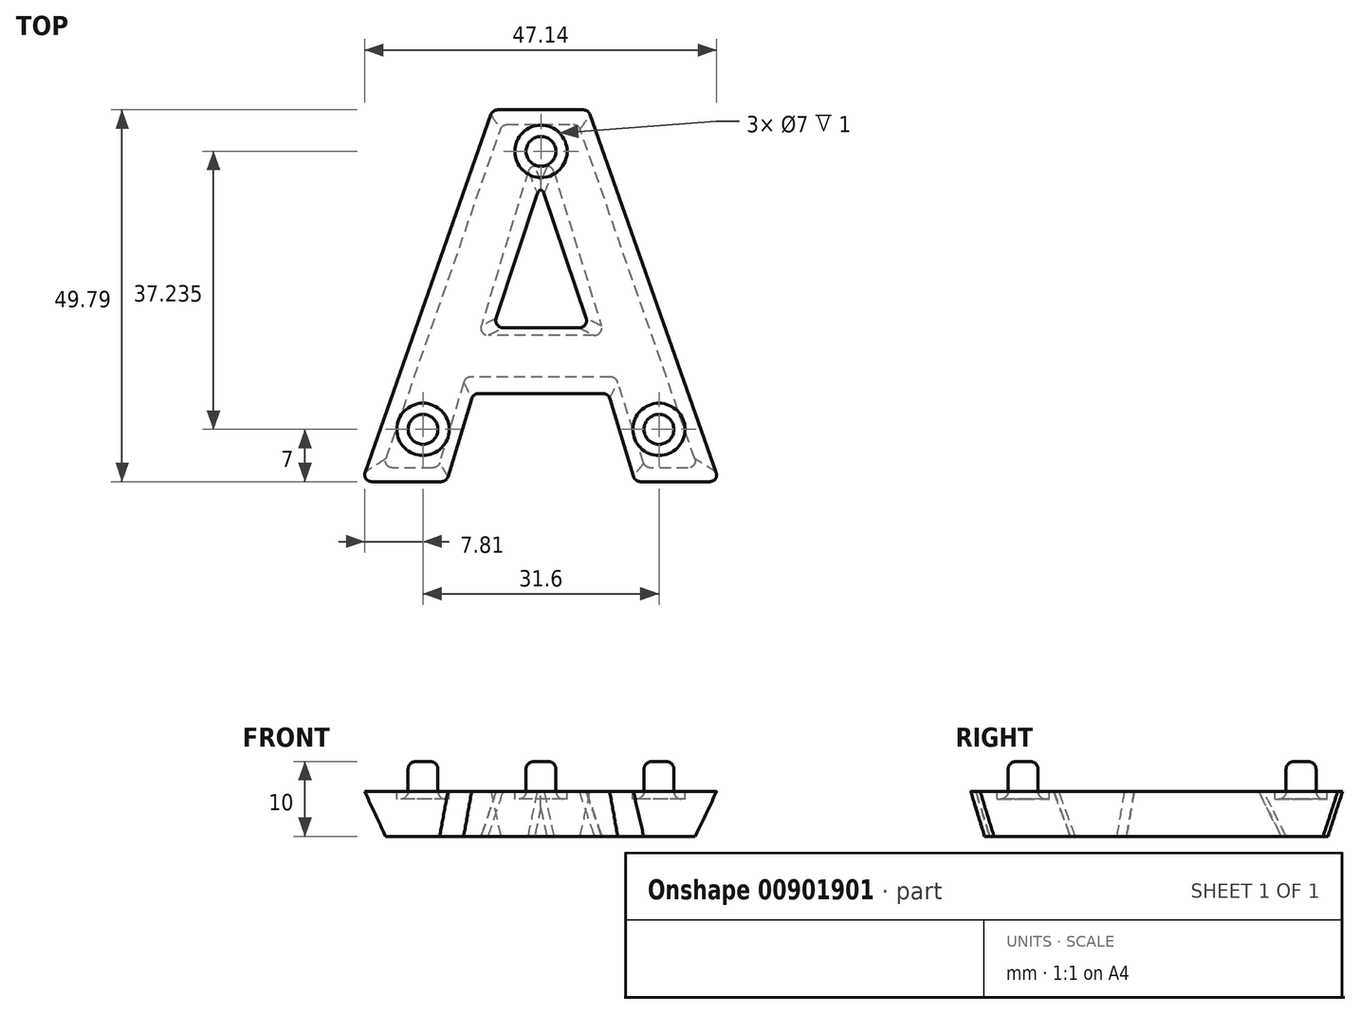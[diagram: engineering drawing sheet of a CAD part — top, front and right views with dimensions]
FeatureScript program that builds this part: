
annotation { "Feature Type Name" : "Feature", "Feature Type Description" : "" }
export const myFeature = defineFeature(function(context is Context, id is Id, definition is map)
    precondition{}
    {
        {
            var Q0;
            Q0=qCreatedBy(makeId("Top.planeOp"),FACE);
            cPlane(context, id + "F0", {"entities" : qUnion([Q0]), "cplaneType" : CPlaneType.OFFSET, "offset" : 6 * mm, "width" : 150 * mm, "height" : 150 * mm});
        }
        {
            var Q0;
            Q0=qCreatedBy(id+"F0.planeOp",FACE);
            var sketch = newSketch(context, id + "F1", { "sketchPlane" : qUnion([Q0])});
            skLineSegment(sketch, "E0", {"start": v(0, 0) * mm, "end": v(17.51, 49.8) * mm});
            skLineSegment(sketch, "E1", {"start": v(17.51, 49.8) * mm, "end": v(30.34, 49.8) * mm});
            skLineSegment(sketch, "E2", {"start": v(30.34, 49.8) * mm, "end": v(47.92, 0) * mm});
            skLineSegment(sketch, "E3", {"start": v(47.92, 0) * mm, "end": v(36.59, 0) * mm});
            skLineSegment(sketch, "E4", {"start": v(36.59, 0) * mm, "end": v(33, 11.8) * mm});
            skLineSegment(sketch, "E5", {"start": v(33, 11.8) * mm, "end": v(14.92, 11.8) * mm});
            skLineSegment(sketch, "E6", {"start": v(14.92, 11.8) * mm, "end": v(11.34, 0) * mm});
            skLineSegment(sketch, "E7", {"start": v(11.34, 0) * mm, "end": v(0, 0) * mm});
            skPoint(sketch, "E8.end.orphan", {"position": v(23.97, 42.08) * mm});
            skSolve(sketch);
        }
        {
            var Q0;
            Q0=qCreatedBy(makeId("Top.planeOp"),FACE);
            var sketch = newSketch(context, id + "F2", { "sketchPlane" : qUnion([Q0])});
            skLineSegment(sketch, "E9", {"start": v(45.03, 1.84) * mm, "end": v(37.97, 1.84) * mm});
            skLineSegment(sketch, "E10", {"start": v(37.97, 1.84) * mm, "end": v(34.05, 14) * mm});
            skLineSegment(sketch, "E11", {"start": v(34.05, 14) * mm, "end": v(13.85, 14) * mm});
            skLineSegment(sketch, "E12", {"start": v(13.85, 14) * mm, "end": v(10.22, 1.84) * mm});
            skLineSegment(sketch, "E13", {"start": v(10.22, 1.84) * mm, "end": v(2.8, 1.84) * mm});
            skLineSegment(sketch, "E14", {"start": v(2.8, 1.84) * mm, "end": v(18.82, 47.84) * mm});
            skLineSegment(sketch, "E15", {"start": v(18.82, 47.84) * mm, "end": v(29.02, 47.84) * mm});
            skLineSegment(sketch, "E16", {"start": v(45.03, 1.84) * mm, "end": v(29.02, 47.84) * mm});
            skLineSegment(sketch, "E17", {"start": v(37.97, 1.84) * mm, "end": v(34.05, 14) * mm, "construction": true});
            skSolve(sketch);
        }
        {
            var Q0;
            Q0=qCreatedBy(id+"F0.planeOp",FACE);
            cPlane(context, id + "F3", {"entities" : qUnion([Q0]), "cplaneType" : CPlaneType.OFFSET, "offset" : 5 * mm, "width" : 150 * mm, "height" : 150 * mm});
        }
        {
            var Q0;
            Q0=qCreatedBy(makeId("Top.planeOp"),FACE);
            cPlane(context, id + "F4", {"entities" : qUnion([Q0]), "cplaneType" : CPlaneType.OFFSET, "offset" : 5 * mm, "oppositeDirection" : true, "width" : 150 * mm, "height" : 150 * mm});
        }
        {
            var Q0;
            Q0=makeQuery(id+"F1.imprint","IMPRINT",FACE,{"disambiguationData":[TD([[makeQuery(id+"F1.imprint","IMPRINT",EDGE,{"derivedFrom":sQuery(id+"F1.wireOp",EDGE,"E0")}),-1.0]])]});
            var Q1;
            Q1=makeQuery(id+"F2.imprint","IMPRINT",FACE,{"disambiguationData":[TD([[makeQuery(id+"F2.imprint","IMPRINT",EDGE,{"derivedFrom":sQuery(id+"F2.wireOp",EDGE,"E9")}),-1.0]])]});
            loft(context, id + "F5", {"sheetProfilesArray" : [{ "sheetProfileEntities" : qUnion([Q0]) }, { "sheetProfileEntities" : qUnion([Q1]) }]});
        }
        {
            var Q0;
            Q0=makeQuery(id+"F1.imprint","IMPRINT",FACE,{"disambiguationData":[TD([[makeQuery(id+"F1.imprint","IMPRINT",EDGE,{"derivedFrom":sQuery(id+"F1.wireOp",EDGE,"E0")}),-1.0]])]});
            var sketch = newSketch(context, id + "F6", { "sketchPlane" : qUnion([Q0])});
            skLineSegment(sketch, "E18", {"start": v(17.57, 20.6) * mm, "end": v(30.48, 20.6) * mm});
            skLineSegment(sketch, "E19", {"start": v(30.48, 20.6) * mm, "end": v(24.2, 39.24) * mm});
            skLineSegment(sketch, "E20", {"start": v(23.75, 39.24) * mm, "end": v(17.57, 20.6) * mm});
            skLineSegment(sketch, "E21", {"start": v(23.75, 39.24) * mm, "end": v(24.2, 39.24) * mm});
            skSolve(sketch);
        }
        {
            var Q0;
            Q0=makeQuery(id+"F2.imprint","IMPRINT",FACE,{"disambiguationData":[TD([[makeQuery(id+"F2.imprint","IMPRINT",EDGE,{"derivedFrom":sQuery(id+"F2.wireOp",EDGE,"E9")}),-1.0]])]});
            var sketch = newSketch(context, id + "F7", { "sketchPlane" : qUnion([Q0])});
            skLineSegment(sketch, "E22", {"start": v(32.48, 19.6) * mm, "end": v(15.62, 19.6) * mm});
            skLineSegment(sketch, "E23", {"start": v(22.5, 42.24) * mm, "end": v(25.5, 42.24) * mm});
            skLineSegment(sketch, "E24", {"start": v(24, 42.24) * mm, "end": v(24, 15.1) * mm, "construction": true});
            skLineSegment(sketch, "E25", {"start": v(25.5, 42.24) * mm, "end": v(37.96, 1.84) * mm, "construction": true});
            skLineSegment(sketch, "E26", {"start": v(22.5, 42.24) * mm, "end": v(8.33, -4.36) * mm, "construction": true});
            skPoint(sketch, "E27.end.orphan", {"position": v(31.77, 19.6) * mm});
            skPoint(sketch, "E28.start.orphan", {"position": v(16.2, 19.6) * mm});
            skLineSegment(sketch, "E29", {"start": v(25.5, 42.24) * mm, "end": v(32.48, 19.6) * mm});
            skLineSegment(sketch, "E30", {"start": v(22.5, 42.24) * mm, "end": v(15.62, 19.6) * mm});
            skSolve(sketch);
        }
        {
            var Q0;
            Q0=makeQuery(id+"F7.imprint","IMPRINT",FACE,{"disambiguationData":[TD([[makeQuery(id+"F7.imprint","IMPRINT",EDGE,{"derivedFrom":sQuery(id+"F7.wireOp",EDGE,"E22")}),-1.0]])]});
            var Q1;
            Q1=makeQuery(id+"F6.imprint","IMPRINT",FACE,{"disambiguationData":[TD([[makeQuery(id+"F6.imprint","IMPRINT",EDGE,{"derivedFrom":sQuery(id+"F6.wireOp",EDGE,"E18")}),1.0]])]});
            loft(context, id + "F8", {"operationType" : NewBodyOperationType.REMOVE, "sheetProfilesArray" : [{ "sheetProfileEntities" : qUnion([Q0]) }, { "sheetProfileEntities" : qUnion([Q1]) }]});
        }
        {
            var Q0;
            Q0=makeQuery(id+"F1.imprint","IMPRINT",FACE,{"disambiguationData":[TD([[makeQuery(id+"F1.imprint","IMPRINT",EDGE,{"derivedFrom":sQuery(id+"F1.wireOp",EDGE,"E0")}),-1.0]])]});
            var sketch = newSketch(context, id + "F9", { "sketchPlane" : qUnion([Q0])});
            skCircle(sketch, "E31", {"center": v(24, 44.24) * mm, "radius": 3.5 * mm});
            skCircle(sketch, "E32", {"center": v(8.2, 7) * mm, "radius": 3.5 * mm});
            skCircle(sketch, "E33", {"center": v(39.8, 7) * mm, "radius": 3.5 * mm});
            skCircle(sketch, "E34", {"center": v(24, 44.24) * mm, "radius": 2 * mm});
            skCircle(sketch, "E35", {"center": v(39.8, 7) * mm, "radius": 2 * mm});
            skCircle(sketch, "E36", {"center": v(8.2, 7) * mm, "radius": 2 * mm});
            skSolve(sketch);
        }
        {
            var Q0;
            Q0=makeQuery(id+"F9.imprint","IMPRINT",FACE,{"disambiguationData":[TD([[makeQuery(id+"F9.imprint","IMPRINT",EDGE,{"derivedFrom":sQuery(id+"F9.wireOp",EDGE,"E36")}),1.0]])]});
            var Q1;
            Q1=makeQuery(id+"F9.imprint","IMPRINT",FACE,{"disambiguationData":[TD([[makeQuery(id+"F9.imprint","IMPRINT",EDGE,{"derivedFrom":sQuery(id+"F9.wireOp",EDGE,"E34")}),1.0]])]});
            var Q2;
            Q2=makeQuery(id+"F9.imprint","IMPRINT",FACE,{"disambiguationData":[TD([[makeQuery(id+"F9.imprint","IMPRINT",EDGE,{"derivedFrom":sQuery(id+"F9.wireOp",EDGE,"E35")}),1.0]])]});
            var Q3;
            Q3=sQuery(id+"F9.wireOp",EDGE,"E36");
            var Q4;
            Q4=sQuery(id+"F9.wireOp",EDGE,"E34");
            var Q5;
            Q5=sQuery(id+"F9.wireOp",EDGE,"E35");
            extrude(context, id + "F10", {"entities" : qUnion([Q0, Q1, Q2]), "operationType" : NewBodyOperationType.ADD, "surfaceEntities" : qUnion([Q3, Q4, Q5]), "depth" : 4 * mm, "offsetDistance" : 25 * mm});
        }
        {
            var Q0;
            Q0=makeQuery(id+"F9.imprint","IMPRINT",FACE,{"disambiguationData":[TD([[makeQuery(id+"F9.imprint","IMPRINT",EDGE,{"derivedFrom":sQuery(id+"F9.wireOp",EDGE,"E32")}),1.0]])]});
            var Q1;
            Q1=sQuery(id+"F9.wireOp",EDGE,"E36");
            var Q2;
            Q2=sQuery(id+"F9.wireOp",EDGE,"E32");
            extrude(context, id + "F11", {"entities" : qUnion([Q0]), "operationType" : NewBodyOperationType.REMOVE, "surfaceEntities" : qUnion([Q1, Q2]), "oppositeDirection" : true, "depth" : 1 * mm, "offsetDistance" : 25 * mm});
        }
        {
            var Q0;
            Q0=makeQuery(id+"F9.imprint","IMPRINT",FACE,{"disambiguationData":[TD([[makeQuery(id+"F9.imprint","IMPRINT",EDGE,{"derivedFrom":sQuery(id+"F9.wireOp",EDGE,"E33")}),1.0]])]});
            var Q1;
            Q1=sQuery(id+"F9.wireOp",EDGE,"E35");
            var Q2;
            Q2=sQuery(id+"F9.wireOp",EDGE,"E33");
            extrude(context, id + "F12", {"entities" : qUnion([Q0]), "operationType" : NewBodyOperationType.REMOVE, "surfaceEntities" : qUnion([Q1, Q2]), "oppositeDirection" : true, "depth" : 1 * mm, "offsetDistance" : 25 * mm});
        }
        {
            var Q0;
            Q0=makeQuery(id+"F9.imprint","IMPRINT",FACE,{"disambiguationData":[TD([[makeQuery(id+"F9.imprint","IMPRINT",EDGE,{"derivedFrom":sQuery(id+"F9.wireOp",EDGE,"E31")}),1.0]])]});
            var Q1;
            Q1=sQuery(id+"F9.wireOp",EDGE,"E34");
            var Q2;
            Q2=sQuery(id+"F9.wireOp",EDGE,"E31");
            extrude(context, id + "F13", {"entities" : qUnion([Q0]), "operationType" : NewBodyOperationType.REMOVE, "surfaceEntities" : qUnion([Q1, Q2]), "oppositeDirection" : true, "depth" : 1 * mm, "offsetDistance" : 25 * mm});
        }
        {
            var Q0;
            Q0=makeQuery(id+"F11.boolean.opBoolean","COPY",EDGE,{"derivedFrom":makeQuery(id+"F11.opExtrude","CAP_EDGE",EDGE,{"disambiguationData":[OSD([sQuery(id+"F9.wireOp",EDGE,"E36")])],"isStart":false})});
            fillet(context, id + "F14", {"entities" : qUnion([Q0]), "tangentPropagation" : true, "radius" : 1 * mm, "defaultsChanged" : false, "vertexSettings" : [], "allowEdgeOverflow" : false});
        }
        {
            var Q0;
            Q0=makeQuery(id+"F10.opExtrude","CAP_EDGE",EDGE,{"disambiguationData":[OSD([sQuery(id+"F9.wireOp",EDGE,"E36")])],"isStart":false});
            fillet(context, id + "F15", {"entities" : qUnion([Q0]), "tangentPropagation" : true, "radius" : 1 * mm, "defaultsChanged" : true, "vertexSettings" : [], "allowEdgeOverflow" : false});
        }
        {
            var Q0;
            Q0=makeQuery(id+"F10.opExtrude","CAP_EDGE",EDGE,{"disambiguationData":[OSD([sQuery(id+"F9.wireOp",EDGE,"E35")])],"isStart":false});
            fillet(context, id + "F16", {"entities" : qUnion([Q0]), "tangentPropagation" : true, "radius" : 1 * mm, "defaultsChanged" : true, "vertexSettings" : [], "allowEdgeOverflow" : false});
        }
        {
            var Q0;
            Q0=makeQuery(id+"F10.opExtrude","CAP_EDGE",EDGE,{"disambiguationData":[OSD([sQuery(id+"F9.wireOp",EDGE,"E34")])],"isStart":false});
            fillet(context, id + "F17", {"entities" : qUnion([Q0]), "tangentPropagation" : true, "radius" : 1 * mm, "defaultsChanged" : true, "vertexSettings" : [], "allowEdgeOverflow" : false});
        }
        {
            var Q0;
            Q0=makeQuery(id+"F13.boolean.opBoolean","COPY",EDGE,{"derivedFrom":makeQuery(id+"F13.opExtrude","CAP_EDGE",EDGE,{"disambiguationData":[OSD([sQuery(id+"F9.wireOp",EDGE,"E34")])],"isStart":false})});
            fillet(context, id + "F18", {"entities" : qUnion([Q0]), "tangentPropagation" : true, "radius" : 1 * mm, "defaultsChanged" : true, "vertexSettings" : [], "allowEdgeOverflow" : false});
        }
        {
            var Q0;
            Q0=makeQuery(id+"F12.boolean.opBoolean","COPY",EDGE,{"derivedFrom":makeQuery(id+"F12.opExtrude","CAP_EDGE",EDGE,{"disambiguationData":[OSD([sQuery(id+"F9.wireOp",EDGE,"E35")])],"isStart":false})});
            fillet(context, id + "F19", {"entities" : qUnion([Q0]), "tangentPropagation" : true, "radius" : 1 * mm, "defaultsChanged" : false, "vertexSettings" : [], "allowEdgeOverflow" : false});
        }
        {
            var Q0;
            Q0=makeQuery(id+"F5.opLoft","MID_CAP_EDGE",EDGE,{"disambiguationData":[OSD([sQuery(id+"F2.wireOp",EDGE,"E9"),sQuery(id+"F2.wireOp",EDGE,"E15"),sQuery(id+"F2.wireOp",EDGE,"E16")])],"capPos":1.0});
            var Q1;
            Q1=makeQuery(id+"F5.opLoft","SWEPT_EDGE",EDGE,{"disambiguationData":[OSD([sQuery(id+"F1.wireOp",EDGE,"E1"),sQuery(id+"F1.wireOp",EDGE,"E2"),sQuery(id+"F2.wireOp",EDGE,"E15"),sQuery(id+"F2.wireOp",EDGE,"E16")])]});
            var Q2;
            Q2=makeQuery(id+"F5.opLoft","SWEPT_EDGE",EDGE,{"disambiguationData":[OSD([sQuery(id+"F1.wireOp",EDGE,"E0"),sQuery(id+"F1.wireOp",EDGE,"E1"),sQuery(id+"F2.wireOp",EDGE,"E14"),sQuery(id+"F2.wireOp",EDGE,"E15")])]});
            var Q3;
            Q3=makeQuery(id+"F5.opLoft","MID_CAP_EDGE",EDGE,{"disambiguationData":[OSD([sQuery(id+"F2.wireOp",EDGE,"E14"),sQuery(id+"F2.wireOp",EDGE,"E15"),sQuery(id+"F2.wireOp",EDGE,"E16")])],"capPos":1.0});
            var Q4;
            Q4=makeQuery(id+"F5.opLoft","MID_CAP_EDGE",EDGE,{"disambiguationData":[OSD([sQuery(id+"F2.wireOp",EDGE,"E13"),sQuery(id+"F2.wireOp",EDGE,"E14"),sQuery(id+"F2.wireOp",EDGE,"E15")])],"capPos":1.0});
            var Q5;
            Q5=makeQuery(id+"F5.opLoft","SWEPT_EDGE",EDGE,{"disambiguationData":[OSD([sQuery(id+"F1.wireOp",EDGE,"E0"),sQuery(id+"F1.wireOp",EDGE,"E7"),sQuery(id+"F2.wireOp",EDGE,"E13"),sQuery(id+"F2.wireOp",EDGE,"E14")])]});
            var Q6;
            Q6=makeQuery(id+"F5.opLoft","MID_CAP_EDGE",EDGE,{"disambiguationData":[OSD([sQuery(id+"F2.wireOp",EDGE,"E12"),sQuery(id+"F2.wireOp",EDGE,"E13"),sQuery(id+"F2.wireOp",EDGE,"E14")])],"capPos":1.0});
            var Q7;
            Q7=makeQuery(id+"F5.opLoft","SWEPT_EDGE",EDGE,{"disambiguationData":[OSD([sQuery(id+"F1.wireOp",EDGE,"E6"),sQuery(id+"F1.wireOp",EDGE,"E7"),sQuery(id+"F2.wireOp",EDGE,"E12"),sQuery(id+"F2.wireOp",EDGE,"E13")])]});
            var Q8;
            Q8=makeQuery(id+"F5.opLoft","MID_CAP_EDGE",EDGE,{"disambiguationData":[OSD([sQuery(id+"F2.wireOp",EDGE,"E11"),sQuery(id+"F2.wireOp",EDGE,"E12"),sQuery(id+"F2.wireOp",EDGE,"E13")])],"capPos":1.0});
            var Q9;
            Q9=makeQuery(id+"F5.opLoft","MID_CAP_EDGE",EDGE,{"disambiguationData":[OSD([sQuery(id+"F2.wireOp",EDGE,"E10"),sQuery(id+"F2.wireOp",EDGE,"E11"),sQuery(id+"F2.wireOp",EDGE,"E12")])],"capPos":1.0});
            var Q10;
            Q10=makeQuery(id+"F5.opLoft","SWEPT_EDGE",EDGE,{"disambiguationData":[OSD([sQuery(id+"F1.wireOp",EDGE,"E5"),sQuery(id+"F1.wireOp",EDGE,"E6"),sQuery(id+"F2.wireOp",EDGE,"E11"),sQuery(id+"F2.wireOp",EDGE,"E12")])]});
            var Q11;
            Q11=makeQuery(id+"F5.opLoft","SWEPT_EDGE",EDGE,{"disambiguationData":[OSD([sQuery(id+"F1.wireOp",EDGE,"E4"),sQuery(id+"F1.wireOp",EDGE,"E5"),sQuery(id+"F2.wireOp",EDGE,"E10"),sQuery(id+"F2.wireOp",EDGE,"E11")])]});
            var Q12;
            Q12=makeQuery(id+"F5.opLoft","MID_CAP_EDGE",EDGE,{"disambiguationData":[OSD([sQuery(id+"F2.wireOp",EDGE,"E9"),sQuery(id+"F2.wireOp",EDGE,"E10"),sQuery(id+"F2.wireOp",EDGE,"E16")])],"capPos":1.0});
            var Q13;
            Q13=makeQuery(id+"F5.opLoft","CAP_FACE",FACE,{"disambiguationData":[OSD([makeQuery(id+"F2.imprint","IMPRINT",FACE,{"disambiguationData":[TD([[makeQuery(id+"F2.imprint","IMPRINT",EDGE,{"derivedFrom":sQuery(id+"F2.wireOp",EDGE,"E9")}),-1.0]])]})])],"isStart":true});
            var Q14;
            Q14=makeQuery(id+"F8.boolean.opBoolean","COPY",EDGE,{"derivedFrom":makeQuery(id+"F8.opLoft","SWEPT_EDGE",EDGE,{"disambiguationData":[OSD([sQuery(id+"F6.wireOp",EDGE,"E19"),sQuery(id+"F6.wireOp",EDGE,"E21"),sQuery(id+"F7.wireOp",EDGE,"E23"),sQuery(id+"F7.wireOp",EDGE,"E29")])]})});
            var Q15;
            Q15=makeQuery(id+"F8.boolean.opBoolean","COPY",EDGE,{"derivedFrom":makeQuery(id+"F8.opLoft","SWEPT_EDGE",EDGE,{"disambiguationData":[OSD([sQuery(id+"F6.wireOp",EDGE,"E20"),sQuery(id+"F6.wireOp",EDGE,"E21"),sQuery(id+"F7.wireOp",EDGE,"E23"),sQuery(id+"F7.wireOp",EDGE,"E30")])]})});
            var Q16;
            Q16=makeQuery(id+"F8.boolean.opBoolean","COPY",EDGE,{"derivedFrom":makeQuery(id+"F8.opLoft","SWEPT_EDGE",EDGE,{"disambiguationData":[OSD([sQuery(id+"F6.wireOp",EDGE,"E18"),sQuery(id+"F6.wireOp",EDGE,"E19"),sQuery(id+"F7.wireOp",EDGE,"E22"),sQuery(id+"F7.wireOp",EDGE,"E29")])]})});
            var Q17;
            Q17=makeQuery(id+"F8.boolean.opBoolean","COPY",EDGE,{"derivedFrom":makeQuery(id+"F8.opLoft","SWEPT_EDGE",EDGE,{"disambiguationData":[OSD([sQuery(id+"F6.wireOp",EDGE,"E18"),sQuery(id+"F6.wireOp",EDGE,"E20"),sQuery(id+"F7.wireOp",EDGE,"E22"),sQuery(id+"F7.wireOp",EDGE,"E30")])]})});
            var Q18;
            Q18=makeQuery(id+"F5.opLoft","SWEPT_EDGE",EDGE,{"disambiguationData":[OSD([sQuery(id+"F1.wireOp",EDGE,"E2"),sQuery(id+"F1.wireOp",EDGE,"E3"),sQuery(id+"F2.wireOp",EDGE,"E9"),sQuery(id+"F2.wireOp",EDGE,"E16")])]});
            var Q19;
            Q19=makeQuery(id+"F5.opLoft","SWEPT_EDGE",EDGE,{"disambiguationData":[OSD([sQuery(id+"F1.wireOp",EDGE,"E3"),sQuery(id+"F1.wireOp",EDGE,"E4"),sQuery(id+"F2.wireOp",EDGE,"E9"),sQuery(id+"F2.wireOp",EDGE,"E10")])]});
            fillet(context, id + "F20", {"entities" : qUnion([Q0, Q1, Q2, Q3, Q4, Q5, Q6, Q7, Q8, Q9, Q10, Q11, Q12, Q13, Q14, Q15, Q16, Q17, Q18, Q19]), "tangentPropagation" : true, "radius" : 1 * mm, "defaultsChanged" : false, "vertexSettings" : [], "allowEdgeOverflow" : false});
        }
    });
